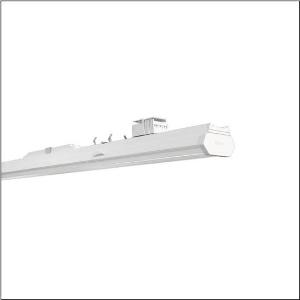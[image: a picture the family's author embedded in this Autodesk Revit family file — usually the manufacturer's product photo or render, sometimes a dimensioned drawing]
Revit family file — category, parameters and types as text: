
# Revit family: licross_r__21_protected_ho_52td12mn4e5m_88f3
name_source: partatom
category: Lighting Fixtures
units: mm (PartAtom-declared; Revit-internal decimal feet)

## family parameters
Cut with Voids When Loaded = No
Host = Face
Light Source = No
Part Type = Normal
Room Calculation Point = No
Round Connector Dimension = Use Diameter
Shared = No

## types (1)
- --- (1 x LED, 14780 lm, 83.2 W, 4000K)
    Apparent Load = 83 VA
    CIE Flux Codes = 70 91 97 98 100
    Color Rendering = 80
    Color Temperature = 4000K
    Default Elevation = 1800 mm
    Description = Licross® 21 Protected HO, luminaire insert, of sheet steel, galvanised, coil coated, white, length: 1.500mm, width: 90mm, height: 101mm, LED rated luminous flux: 14.790lm, light colour: 840, control gear: ON/OFF Multilumen, with plug, 3-pole, with phase selection, mains connection: 220..240V, AC, 50/60Hz, rated input power: 83W, halogen-free wiring, primary light control with lens, of plastic, primary optical cover: cover, of PMMA, light emission: direct distribution, primary light characteristic: symmetric, protection rating (complete): IP54, insulation class (complete): insulation class I (protective earthing), certification: CE, ENEC, VDE, UKCA, protection symbol: D if used in an environment with non-conductive dust loads with corresponding accessories, impact resistance: IK06, permissible ambient temperature for indoor applications: -35..+35°C, corresponds to IFS (International Featured Standards) requirements for safety and quality in the food industry, reducing of maximum allowable ambient temperature of 5°C with ceiling mounting, LABS conformity tested according to VDMA 24364:2018-05, packaging unit: 1 piece
    Height = 92 mm
    Lamp = 1 x LED
    Lamp Light Flux = 14780 lm
    Lamp Power = 83.2 W
    Lamp count = 1
    Length = 1500 mm
    Luminous efficacy = 178 lm/W
    Manufacturer = Siteco
    ModVariant = No
    Model = 52TD12MN4E5M
    Mounting Place = Ceiling
    Mounting Type = Pendant
    Number of Poles = 1
    OnlyDefault = Yes
    Power Factor = 1
    Product Name = Licross® 21 Protected HO
    Product group = luminaire insert
    ProductGroupID = 901
    Protection Class = Protection class I
    Protection Degree = IP 54
    RLX_Detail_Level = 1
    RLX_Emergency_Light_Flux = 0 lm
    RLX_Emergency_Type = 0
    RLX_Emergency_Type_DB = No
    RlxData = <blob elided: 22121 chars, md5=f16155ea>
    Socket = socket
    Standby Power = 0 W
    System Light Flux = 14780 lm
    System Power = 83 W
    Type Comments = factory setting: luminous flux: 100 % | (A | C | E) | 195 mA
    Type Image = l_1256148.jpg
    URL = http://relux.com
    VarID = @adj_078021
    Voltage = 0 V
    Weight = 0.00 kg
    Width = 88 mm

## geometry (parser evidence)
native form markers: Blend x4, Sweep x12
no freeform markers — native parametric forms only
